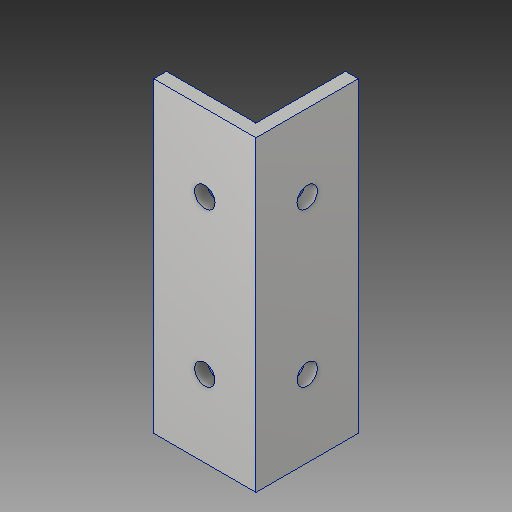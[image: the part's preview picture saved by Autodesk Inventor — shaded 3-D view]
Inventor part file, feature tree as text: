
AUTODESK INVENTOR PART (.ipt)
format: ipt  version: 2018 (Build 220112000, 112)  size: 121,856 bytes
history: native  units: in
note: dims shown in document units (in); Inventor stores cm internally (conversion verified against a paired STEP export)
features: extrude x3, sketch x3
ambient origin geometry x8: Origin, YZ Plane, XZ Plane, XY Plane, X Axis, Y Axis, Z Axis, Center Point
bodies: Solid1 (feature_tree)
feature tree (6):
  extrude  "Extrusion1"  Depth=0.125in
  extrude  "Extrusion2"  Depth=0.125in
  extrude  "Extrusion3"  Depth=1.0in
  sketch  "Sketch1"  dims[d0=1.0in d1=0.125in]
  sketch  "Sketch2"  dims[d2=1.0in d3=0.125in]
  sketch  "Sketch3"  dims[d4=3.0in d5=0.0in d6=0.5in d7=0.75in d8=0.75in d9=0.2in d10=1.0in d11=0.0in d12=0.75in d13=0.75in d14=0.2in d15=1.0in d16=0.0in]
